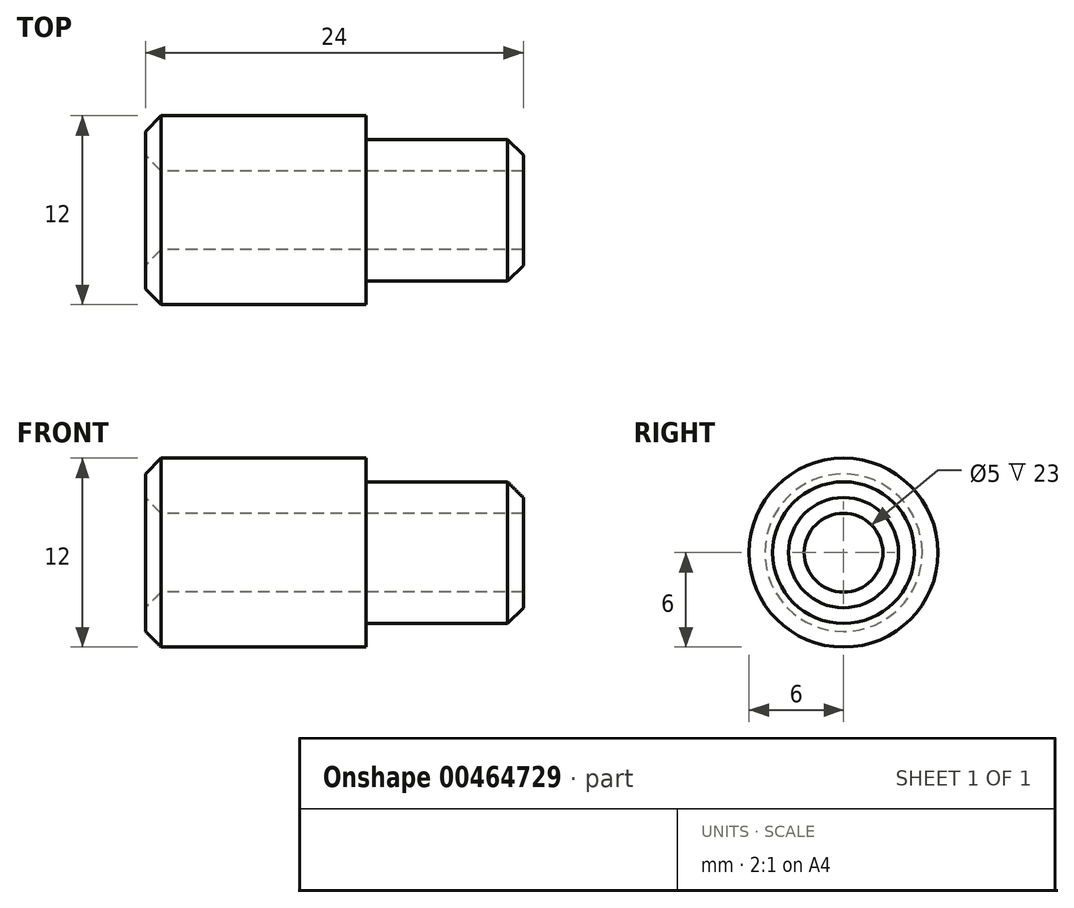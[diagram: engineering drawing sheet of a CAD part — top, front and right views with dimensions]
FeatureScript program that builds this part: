
annotation { "Feature Type Name" : "Feature", "Feature Type Description" : "" }
export const myFeature = defineFeature(function(context is Context, id is Id, definition is map)
    precondition{}
    {
        {
            var Q0;
            Q0=qCreatedBy(makeId("Front.planeOp"),FACE);
            var sketch = newSketch(context, id + "F0", { "sketchPlane" : qUnion([Q0])});
            skLineSegment(sketch, "E0", {"start": v(0, 2.5) * mm, "end": v(24, 2.5) * mm});
            skLineSegment(sketch, "E1", {"start": v(24, 2.5) * mm, "end": v(24, 4.5) * mm});
            skLineSegment(sketch, "E2", {"start": v(24, 4.5) * mm, "end": v(14, 4.5) * mm});
            skLineSegment(sketch, "E3", {"start": v(14, 4.5) * mm, "end": v(14, 6) * mm});
            skLineSegment(sketch, "E4", {"start": v(14, 6) * mm, "end": v(0, 6) * mm});
            skLineSegment(sketch, "E5", {"start": v(0, 6) * mm, "end": v(0, 2.5) * mm});
            skSolve(sketch);
        }
        {
            var Q0;
            Q0=qCreatedBy(makeId("Front.planeOp"),FACE);
            var sketch = newSketch(context, id + "F1", { "sketchPlane" : qUnion([Q0])});
            skLineSegment(sketch, "E6", {"start": v(0.55, 0) * mm, "end": v(37.11, 0) * mm});
            skSolve(sketch);
        }
        {
            var Q0;
            Q0=makeQuery(id+"F0.imprint","IMPRINT",FACE,{"disambiguationData":[TD([[makeQuery(id+"F0.imprint","IMPRINT",EDGE,{"derivedFrom":sQuery(id+"F0.wireOp",EDGE,"E0")}),1.0]])]});
            var Q1;
            Q1=sQuery(id+"F1.wireOp",EDGE,"E6");
            revolve(context, id + "F2", {"entities" : qUnion([Q0]), "axis" : qUnion([Q1]), "revolveType" : RevolveType.FULL});
        }
        {
            var Q0;
            Q0=makeQuery(id+"F2.opRevolve","SWEPT_EDGE",EDGE,{"disambiguationData":[OSD([sQuery(id+"F0.wireOp",EDGE,"E1"),sQuery(id+"F0.wireOp",EDGE,"E2")])]});
            var Q1;
            Q1=makeQuery(id+"F2.opRevolve","SWEPT_EDGE",EDGE,{"disambiguationData":[OSD([sQuery(id+"F0.wireOp",EDGE,"E4"),sQuery(id+"F0.wireOp",EDGE,"E5")])]});
            var Q2;
            Q2=makeQuery(id+"F2.opRevolve","SWEPT_EDGE",EDGE,{"disambiguationData":[OSD([sQuery(id+"F0.wireOp",EDGE,"E0"),sQuery(id+"F0.wireOp",EDGE,"E5")])]});
            chamfer(context, id + "F3", {"entities" : qUnion([Q0, Q1, Q2]), "width" : 1 * mm, "tangentPropagation" : true});
        }
    });
